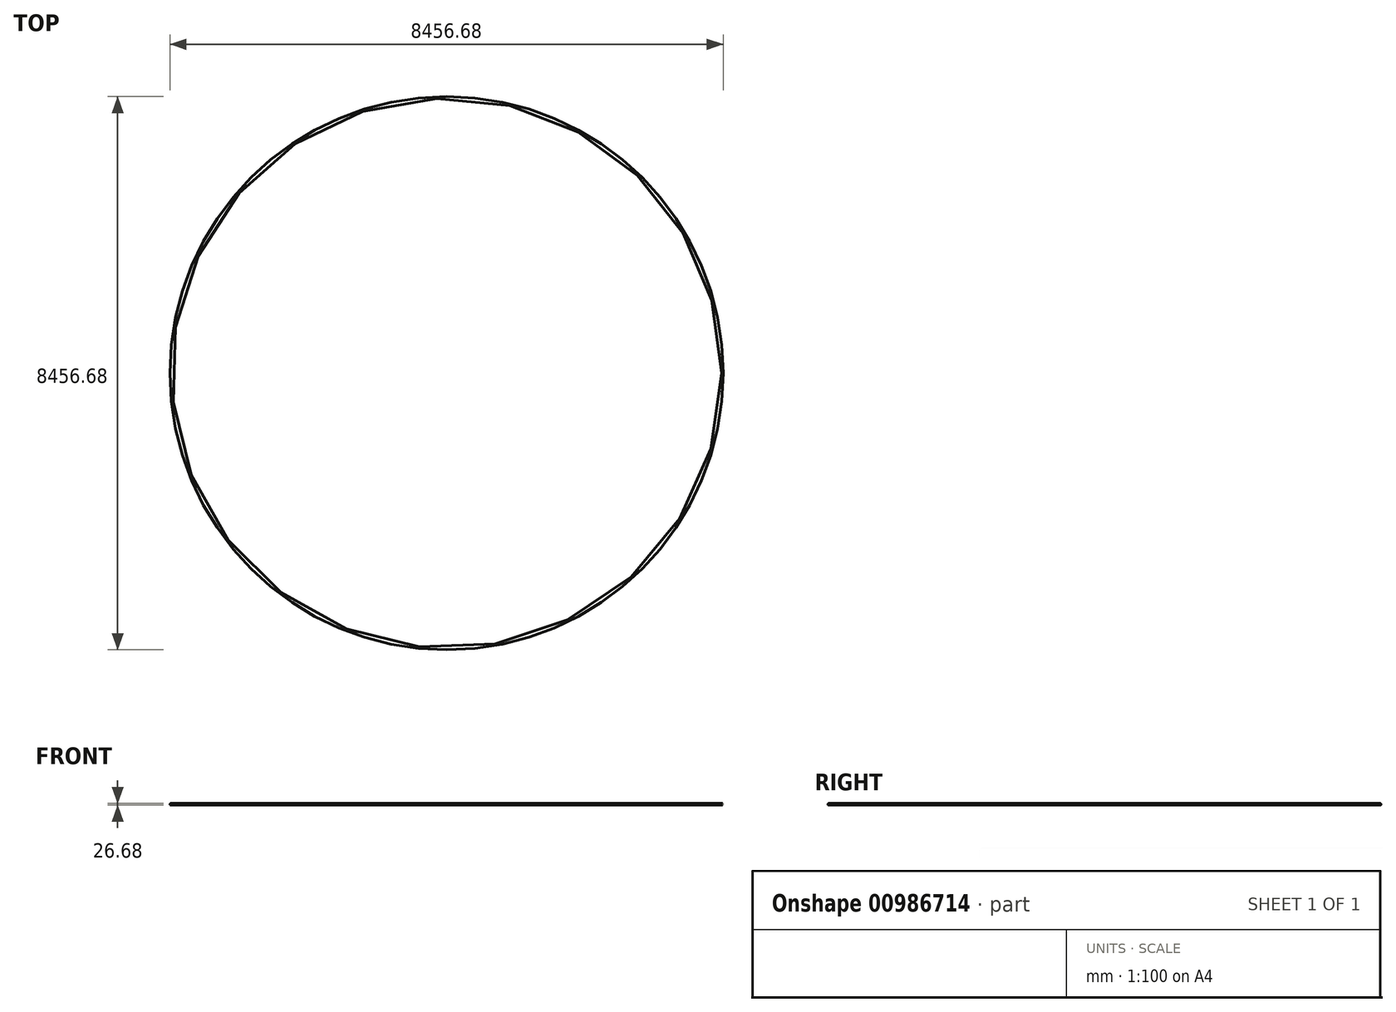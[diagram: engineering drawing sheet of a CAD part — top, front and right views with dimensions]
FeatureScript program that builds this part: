
annotation { "Feature Type Name" : "Feature", "Feature Type Description" : "" }
export const myFeature = defineFeature(function(context is Context, id is Id, definition is map)
    precondition{}
    {
        {
            var Q0;
            Q0=qCreatedBy(makeId("Front.planeOp"),FACE);
            var sketch = newSketch(context, id + "F0", { "sketchPlane" : qUnion([Q0])});
            skLineSegment(sketch, "E0", {"start": v(0, 0) * mm, "end": v(-4215, 0) * mm, "construction": true});
            skCircle(sketch, "E1", {"center": v(-4215, 0) * mm, "radius": 13.33 * mm});
            skCircle(sketch, "E2.0", {"center": v(-4215, 0) * mm, "radius": 11.23 * mm});
            skLineSegment(sketch, "E3", {"start": v(0, 0) * mm, "end": v(0, -25) * mm, "construction": true});
            skSolve(sketch);
        }
        {
            var Q0;
            Q0=makeQuery(id+"F0.imprint","IMPRINT",FACE,{"disambiguationData":[TD([[makeQuery(id+"F0.imprint","IMPRINT",EDGE,{"derivedFrom":sQuery(id+"F0.wireOp",EDGE,"E1")}),1.0]])]});
            var Q1;
            Q1=sQuery(id+"F0.wireOp",EDGE,"E3");
            revolve(context, id + "F1", {"surfaceOperationType" : NewSurfaceOperationType.NEW, "entities" : qUnion([Q0]), "axis" : qUnion([Q1]), "revolveType" : RevolveType.FULL});
        }
    });
